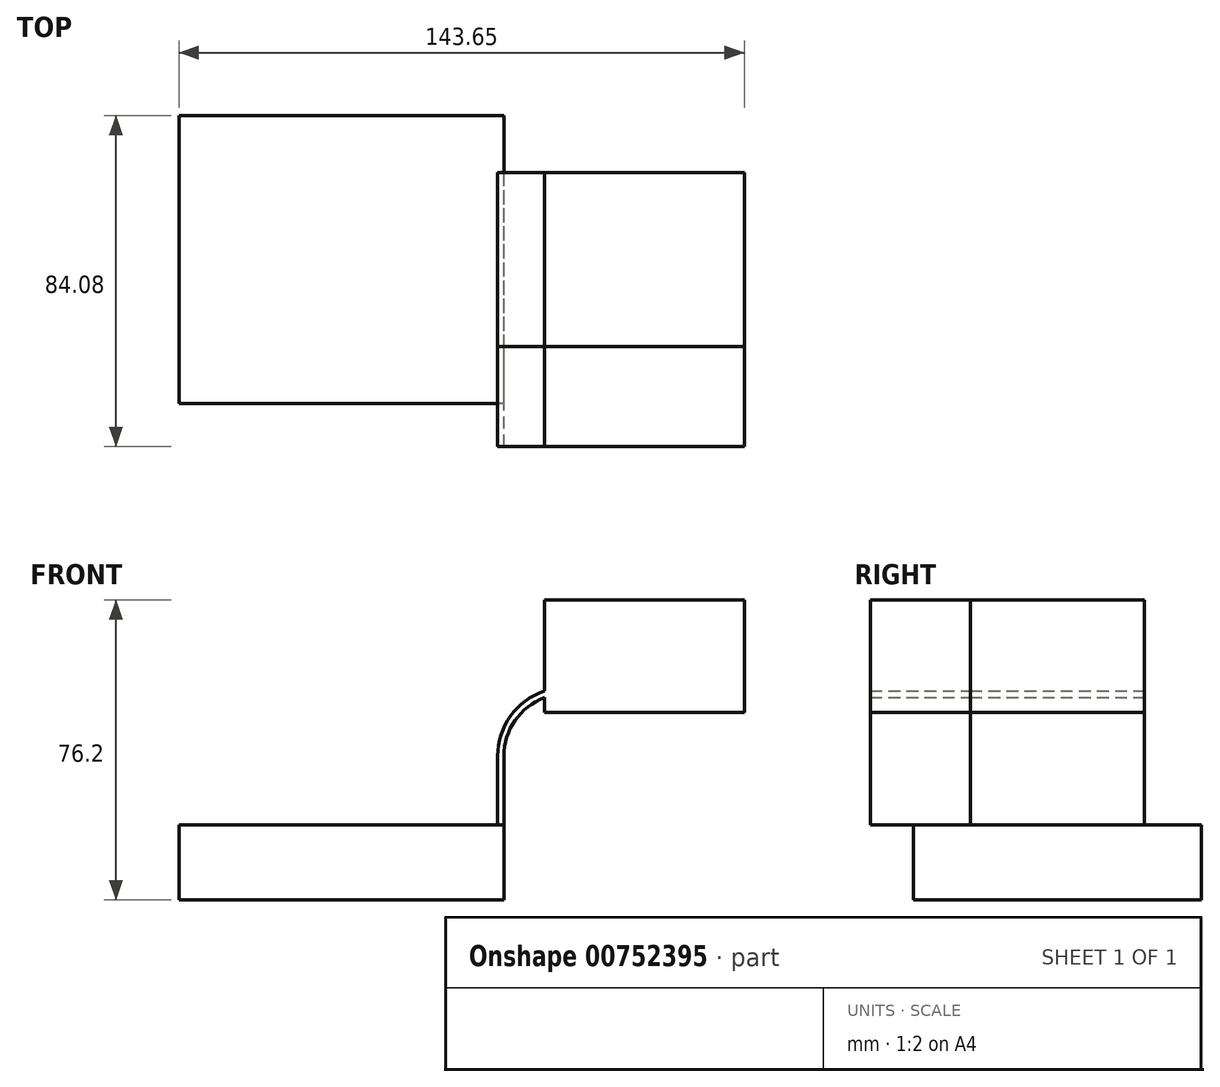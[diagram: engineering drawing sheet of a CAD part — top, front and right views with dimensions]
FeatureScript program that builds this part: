
annotation { "Feature Type Name" : "Feature", "Feature Type Description" : "" }
export const myFeature = defineFeature(function(context is Context, id is Id, definition is map)
    precondition{}
    {
        {
            var Q0;
            Q0=qCreatedBy(makeId("Front.planeOp"),FACE);
            var sketch = newSketch(context, id + "F0", { "sketchPlane" : qUnion([Q0])});
            skLineSegment(sketch, "E0.bottom", {"start": v(41.28, -9.52) * mm, "end": v(-41.28, -9.53) * mm});
            skLineSegment(sketch, "E0.top", {"start": v(41.28, 9.53) * mm, "end": v(-41.28, 9.53) * mm});
            skLineSegment(sketch, "E0.left", {"start": v(41.28, -9.52) * mm, "end": v(41.28, 9.53) * mm});
            skLineSegment(sketch, "E0.right", {"start": v(-41.28, -9.53) * mm, "end": v(-41.28, 9.53) * mm});
            skPoint(sketch, "E0.middle", {"position": v(0, 0) * mm});
            skLineSegment(sketch, "E1.bottom", {"start": v(51.58, 66.68) * mm, "end": v(102.38, 66.68) * mm});
            skLineSegment(sketch, "E1.top", {"start": v(51.58, 38.1) * mm, "end": v(102.38, 38.1) * mm});
            skLineSegment(sketch, "E1.left", {"start": v(51.58, 66.68) * mm, "end": v(51.58, 38.1) * mm});
            skLineSegment(sketch, "E1.right", {"start": v(102.38, 66.68) * mm, "end": v(102.38, 38.1) * mm});
            skLineSegment(sketch, "E2", {"start": v(41.28, 9.53) * mm, "end": v(41.28, 27) * mm});
            skArc(sketch, "E3", {"start": v(41.27, 27) * mm, "mid": v(45.92, 38.23) * mm, "end": v(57.15, 42.88) * mm});
            skLineSegment(sketch, "E4", {"start": v(57.15, 42.88) * mm, "end": v(85.72, 42.88) * mm});
            skLineSegment(sketch, "E5.0", {"start": v(57.15, 44.46) * mm, "end": v(85.72, 44.46) * mm});
            skArc(sketch, "E5.1", {"start": v(39.69, 27) * mm, "mid": v(44.8, 39.35) * mm, "end": v(57.15, 44.46) * mm});
            skLineSegment(sketch, "E5.2", {"start": v(39.69, 9.53) * mm, "end": v(39.69, 27) * mm});
            skSolve(sketch);
        }
        {
            var Q0;
            Q0=makeQuery(id+"F0.imprint","IMPRINT",FACE,{"disambiguationData":[TD([[makeQuery(id+"F0.imprint","IMPRINT",EDGE,{"derivedFrom":sQuery(id+"F0.wireOp",EDGE,"E0.bottom")}),-1.0]])]});
            extrude(context, id + "F1", {"entities" : qUnion([Q0]), "endBound" : BoundingType.SYMMETRIC, "depth" : 73.15 * mm, "offsetDistance" : 25.4 * mm});
        }
        {
            var Q0;
            {var subQ3=sQuery(id+"F0.wireOp",EDGE,"E1.bottom");Q0=makeQuery(id+"F0.imprint","IMPRINT",FACE,{"disambiguationData":[TD([[makeQuery(id+"F0.imprint","IMPRINT",EDGE,{"derivedFrom":subQ3}),-1.0]])]});}
            var Q1;
            {var subQ1=sQuery(id+"F0.wireOp",EDGE,"E2");Q1=makeQuery(id+"F0.imprint","IMPRINT",FACE,{"disambiguationData":[TD([[makeQuery(id+"F0.imprint","IMPRINT",EDGE,{"derivedFrom":subQ1}),1.0]])]});}
            extrude(context, id + "F2", {"entities" : qUnion([Q0, Q1]), "endBound" : BoundingType.SYMMETRIC, "depth" : 44.2 * mm, "offsetDistance" : 25.4 * mm});
        }
        {
            var Q0;
            Q0=makeQuery(id+"F2.opExtrude","CAP_FACE",FACE,{"disambiguationData":[OSD([sQuery(id+"F0.wireOp",EDGE,"E0.top"),sQuery(id+"F0.wireOp",EDGE,"E1.bottom"),sQuery(id+"F0.wireOp",EDGE,"E1.top"),sQuery(id+"F0.wireOp",EDGE,"E1.left"),sQuery(id+"F0.wireOp",EDGE,"E1.right"),sQuery(id+"F0.wireOp",EDGE,"E2"),sQuery(id+"F0.wireOp",EDGE,"E3"),sQuery(id+"F0.wireOp",EDGE,"E5.1"),sQuery(id+"F0.wireOp",EDGE,"E5.2")])],"isStart":false});
            extrude(context, id + "F3", {"entities" : qUnion([Q0]), "depth" : 25.4 * mm, "offsetDistance" : 25.4 * mm});
        }
    });
